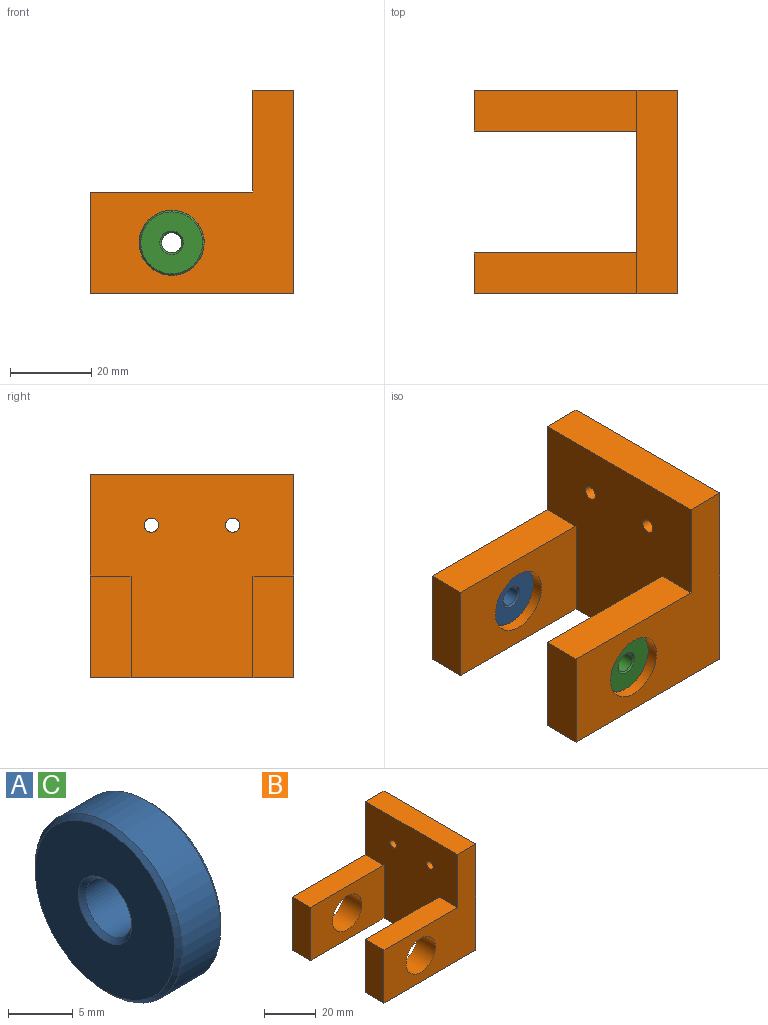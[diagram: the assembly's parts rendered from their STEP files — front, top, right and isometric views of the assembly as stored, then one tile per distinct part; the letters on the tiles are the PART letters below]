
ASSEMBLY  parts=3 mates=2
PART A: 8 faces, bbox 5x16x16 mm
  f0: cylinder r=2.5mm len=5mm, axis (1,0,0), area 66mm2, adj f4,f7
  f1: plane 15.2x15.2mm, normal (-1,0,0), area 155mm2, adj f4,f5
  f2: plane 15.2x15.2mm, normal (1,0,0), area 155mm2, adj f6,f7
  f3: cylinder r=8mm len=16mm, axis (1,0,0), area 211.1mm2, adj f5,f6
  f4: cone r=2.5mm half-angle=45deg, axis (-1,0,0), area 9.6mm2, adj f0,f1
  f5: cone r=8mm half-angle=45deg, axis (1,0,0), area 27.7mm2, adj f1,f3
  f6: cone r=8mm half-angle=45deg, axis (-1,0,0), area 27.7mm2, adj f2,f3
  f7: cone r=2.9mm half-angle=45deg, axis (1,0,0), area 9.6mm2, adj f0,f2
PART B: 16 faces, bbox 50x50x50 mm
  f0: cylinder r=8mm len=16mm, axis (0,1,0), area 502.7mm2, adj f4,f8
  f1: plane 25x10mm, normal (-1,0,0), area 250mm2, adj f4,f5,f8,f9
  f2: plane 25x10mm, normal (-1,0,0), area 250mm2, adj f6,f7,f9,f10
  f3: cylinder r=8mm len=16mm, axis (0,1,0), area 502.7mm2, adj f7,f10
  f4: plane 40x25mm, normal (0,-1,0), area 798.9mm2, adj f0,f1,f5,f9,f13
  f5: plane 40x10mm, normal (0,0,1), area 400mm2, adj f1,f4,f8,f13
  f6: plane 40x10mm, normal (0,0,1), area 400mm2, adj f2,f7,f10,f13
  f7: plane 40x25mm, normal (0,1,0), area 798.9mm2, adj f2,f3,f6,f9,f13
  f8: plane 50x50mm, normal (0,1,0), area 1298.9mm2, adj f0,f1,f5,f9,f11,f13,f14
  f9: plane 50x50mm, normal (0,0,-1), area 1300mm2, adj f1,f2,f4,f7,f8,f10,f13,f14
  f10: plane 50x50mm, normal (0,-1,0), area 1298.9mm2, adj f2,f3,f6,f9,f11,f13,f14
  f11: plane 50x10mm, normal (0,0,1), area 500mm2, adj f8,f10,f13,f14
  f12: cylinder r=1.75mm len=10mm, axis (-1,0,0), area 110mm2, adj f13,f14
  f13: plane 50x50mm, normal (-1,0,0), area 1980.8mm2, adj f4,f5,f6,f7,f8,f9,f10,f11
  f14: plane 50x50mm, normal (1,0,0), area 2480.8mm2, adj f8,f9,f10,f11,f12,f15
  f15: cylinder r=1.75mm len=10mm, axis (-1,0,0), area 110mm2, adj f13,f14
PART C: same geometry as A
PLACE A rot(axis=(-0.58,-0.58,0.58),120deg) t=(34.89,-2.39,23.4)mm
PLACE B t=(39.89,0.11,23.4)mm
PLACE C rot(axis=(0.58,0.58,0.58),120deg) t=(34.89,-42.39,23.4)mm
MATE fastened C.f0 <-> B.f0  axis (0,-1,0) through (34.89,-47.39,23.4)mm
MATE fastened A.f0 <-> B.f0  axis (0,-1,0) through (34.89,-7.39,23.4)mm
